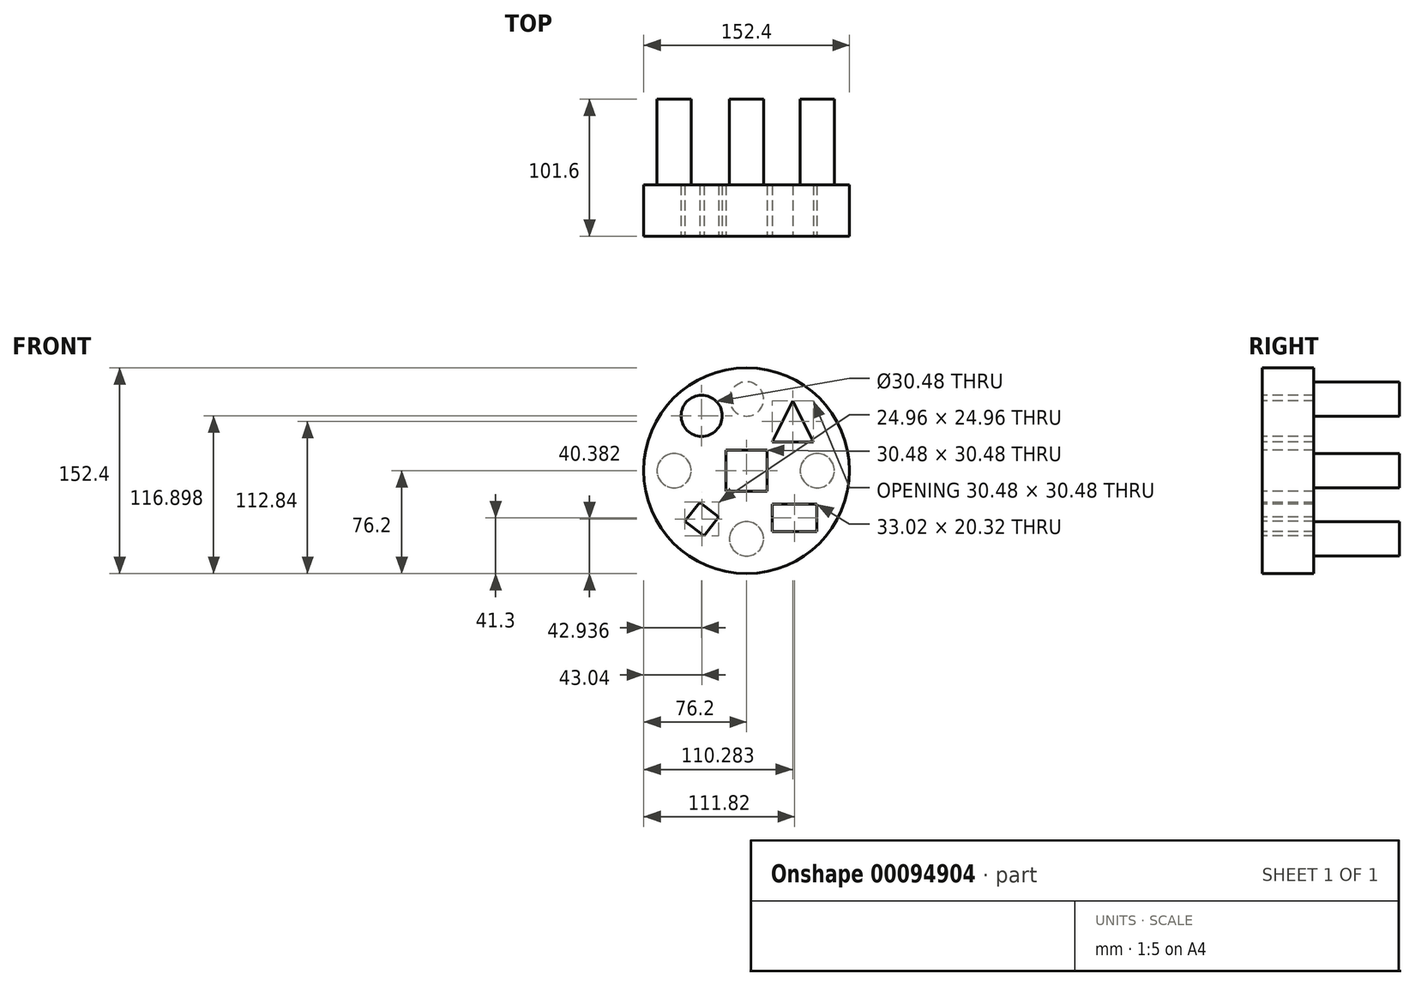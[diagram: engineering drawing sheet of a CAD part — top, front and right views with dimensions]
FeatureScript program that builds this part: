
annotation { "Feature Type Name" : "Feature", "Feature Type Description" : "" }
export const myFeature = defineFeature(function(context is Context, id is Id, definition is map)
    precondition{}
    {
        {
            var Q0;
            Q0=qCreatedBy(makeId("Front.planeOp"),FACE);
            var sketch = newSketch(context, id + "F0", { "sketchPlane" : qUnion([Q0])});
            skCircle(sketch, "E0", {"center": v(0, 0) * mm, "radius": 76.2 * mm});
            skSolve(sketch);
        }
        {
            var Q0;
            Q0 = qSketchRegion(id + "F0", true);
            extrude(context, id + "F1", {"entities" : qUnion([Q0]), "depth" : 38.1 * mm});
        }
        {
            var Q0;
            Q0=makeQuery(id+"F1.opExtrude","CAP_FACE",FACE,{"disambiguationData":[OSD([sQuery(id+"F0.wireOp",EDGE,"E0")])],"isStart":false});
            var sketch = newSketch(context, id + "F2", { "sketchPlane" : qUnion([Q0])});
            skLineSegment(sketch, "E1", {"start": v(18.84, 21.4) * mm, "end": v(49.32, 21.4) * mm});
            skLineSegment(sketch, "E2", {"start": v(34.08, 51.88) * mm, "end": v(18.84, 21.4) * mm});
            skLineSegment(sketch, "E3", {"start": v(34.08, 51.88) * mm, "end": v(49.32, 21.4) * mm});
            skSolve(sketch);
        }
        {
            var Q0;
            Q0=makeQuery(id+"F1.opExtrude","CAP_FACE",FACE,{"disambiguationData":[OSD([sQuery(id+"F0.wireOp",EDGE,"E0")])],"isStart":false});
            var sketch = newSketch(context, id + "F3", { "sketchPlane" : qUnion([Q0])});
            skCircle(sketch, "E4", {"center": v(-33.26, 40.7) * mm, "radius": 15.24 * mm});
            skSolve(sketch);
        }
        {
            var Q0;
            Q0 = qSketchRegion(id + "F3", true);
            extrude(context, id + "F4", {"entities" : qUnion([Q0]), "operationType" : NewBodyOperationType.REMOVE, "oppositeDirection" : true, "depth" : 38.1 * mm});
        }
        {
            var Q0;
            Q0=makeQuery(id+"F2.imprint","IMPRINT",FACE,{"disambiguationData":[TD([[makeQuery(id+"F2.imprint","IMPRINT",EDGE,{"derivedFrom":sQuery(id+"F2.wireOp",EDGE,"E1")}),1.0]])]});
            extrude(context, id + "F5", {"entities" : qUnion([Q0]), "operationType" : NewBodyOperationType.REMOVE, "oppositeDirection" : true, "depth" : 50.8 * mm});
        }
        {
            var Q0;
            Q0=makeQuery(id+"F1.opExtrude","CAP_FACE",FACE,{"disambiguationData":[OSD([sQuery(id+"F0.wireOp",EDGE,"E0")])],"isStart":false});
            var sketch = newSketch(context, id + "F6", { "sketchPlane" : qUnion([Q0])});
            skLineSegment(sketch, "E5", {"start": v(0, 15.24) * mm, "end": v(15.24, 15.24) * mm});
            skLineSegment(sketch, "E6", {"start": v(0, 15.24) * mm, "end": v(-15.24, 15.24) * mm});
            skLineSegment(sketch, "E7", {"start": v(0, -15.24) * mm, "end": v(15.24, -15.24) * mm});
            skLineSegment(sketch, "E8", {"start": v(0, -15.24) * mm, "end": v(-15.24, -15.24) * mm});
            skLineSegment(sketch, "E9", {"start": v(-15.24, 15.24) * mm, "end": v(-15.24, -15.24) * mm});
            skLineSegment(sketch, "E10", {"start": v(15.24, -15.24) * mm, "end": v(15.24, 15.24) * mm});
            skSolve(sketch);
        }
        {
            var Q0;
            Q0 = qSketchRegion(id + "F6", true);
            extrude(context, id + "F7", {"entities" : qUnion([Q0]), "operationType" : NewBodyOperationType.REMOVE, "oppositeDirection" : true, "depth" : 38.1 * mm});
        }
        {
            var Q0;
            Q0=makeQuery(id+"F1.opExtrude","CAP_FACE",FACE,{"disambiguationData":[OSD([sQuery(id+"F0.wireOp",EDGE,"E0")])],"isStart":true});
            var sketch = newSketch(context, id + "F8", { "sketchPlane" : qUnion([Q0])});
            skCircle(sketch, "E11", {"center": v(0, 53.11) * mm, "radius": 12.7 * mm});
            skCircle(sketch, "E12", {"center": v(0, -50.53) * mm, "radius": 12.7 * mm});
            skCircle(sketch, "E13", {"center": v(53.68, 0) * mm, "radius": 12.7 * mm});
            skCircle(sketch, "E14", {"center": v(-52.42, 0) * mm, "radius": 12.7 * mm});
            skSolve(sketch);
        }
        {
            var Q0;
            Q0 = qSketchRegion(id + "F8", true);
            extrude(context, id + "F9", {"entities" : qUnion([Q0]), "operationType" : NewBodyOperationType.ADD, "depth" : 63.5 * mm});
        }
        {
            var Q0;
            Q0=makeQuery(id+"F1.opExtrude","CAP_FACE",FACE,{"disambiguationData":[OSD([sQuery(id+"F0.wireOp",EDGE,"E0")])],"isStart":false});
            var sketch = newSketch(context, id + "F10", { "sketchPlane" : qUnion([Q0])});
            skLineSegment(sketch, "E15", {"start": v(19.11, -24.74) * mm, "end": v(52.13, -24.74) * mm});
            skLineSegment(sketch, "E16", {"start": v(52.13, -24.74) * mm, "end": v(52.13, -45.06) * mm});
            skLineSegment(sketch, "E17", {"start": v(52.13, -45.06) * mm, "end": v(19.11, -45.06) * mm});
            skLineSegment(sketch, "E18", {"start": v(19.11, -24.74) * mm, "end": v(19.11, -45.06) * mm});
            skSolve(sketch);
        }
        {
            var Q0;
            Q0 = qSketchRegion(id + "F10", true);
            extrude(context, id + "F11", {"entities" : qUnion([Q0]), "operationType" : NewBodyOperationType.REMOVE, "oppositeDirection" : true, "depth" : 50.8 * mm});
        }
        {
            var Q0;
            Q0=makeQuery(id+"F1.opExtrude","CAP_FACE",FACE,{"disambiguationData":[OSD([sQuery(id+"F0.wireOp",EDGE,"E0")])],"isStart":false});
            var sketch = newSketch(context, id + "F12", { "sketchPlane" : qUnion([Q0])});
            skLineSegment(sketch, "E19", {"start": v(-34.69, -23.34) * mm, "end": v(-45.64, -37.35) * mm});
            skLineSegment(sketch, "E20", {"start": v(-45.64, -37.35) * mm, "end": v(-31.63, -48.3) * mm});
            skLineSegment(sketch, "E21", {"start": v(-31.63, -48.3) * mm, "end": v(-20.68, -34.3) * mm});
            skLineSegment(sketch, "E22", {"start": v(-20.68, -34.3) * mm, "end": v(-34.69, -23.34) * mm});
            skSolve(sketch);
        }
        {
            var Q0;
            Q0 = qSketchRegion(id + "F12", true);
            extrude(context, id + "F13", {"entities" : qUnion([Q0]), "operationType" : NewBodyOperationType.REMOVE, "depth" : 38.1 * mm});
        }
        {
            var Q0;
            Q0 = qSketchRegion(id + "F12", true);
            extrude(context, id + "F14", {"entities" : qUnion([Q0]), "operationType" : NewBodyOperationType.REMOVE, "oppositeDirection" : true, "depth" : 38.1 * mm});
        }
        {
            var Q0;
            Q0 = qSketchRegion(id + "F12", true);
            extrude(context, id + "F15", {"entities" : qUnion([Q0]), "operationType" : NewBodyOperationType.REMOVE, "oppositeDirection" : true, "depth" : 38.1 * mm});
        }
    });
